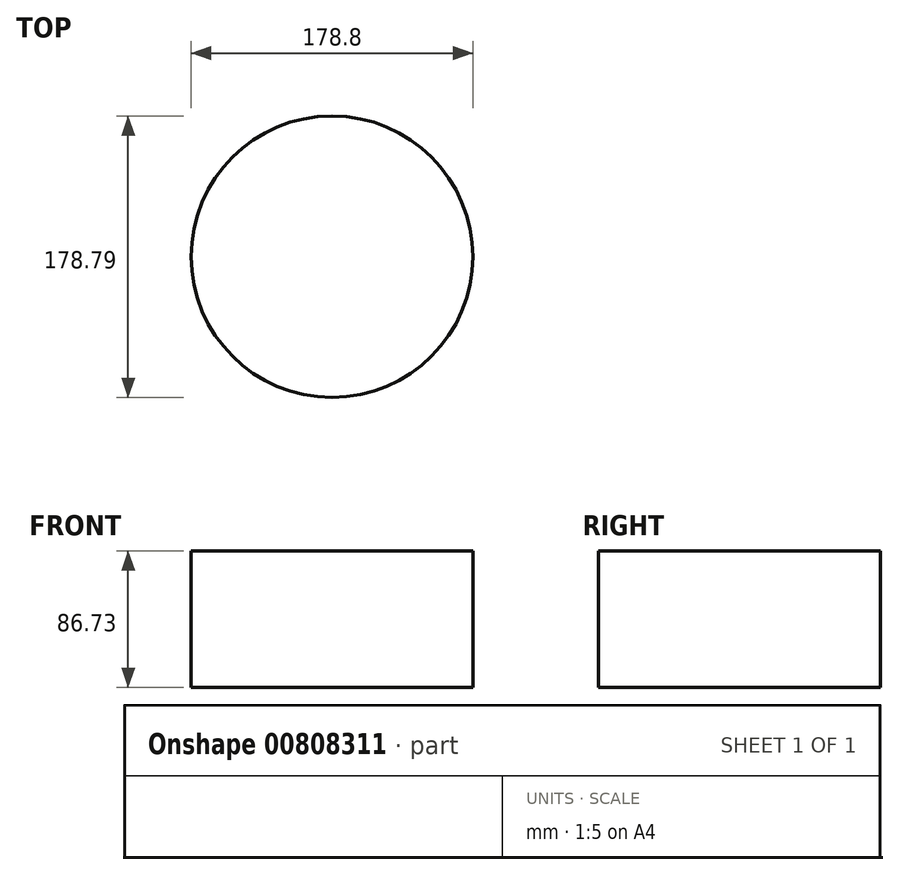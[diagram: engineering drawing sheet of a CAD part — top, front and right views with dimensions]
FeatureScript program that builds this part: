
annotation { "Feature Type Name" : "Feature", "Feature Type Description" : "" }
export const myFeature = defineFeature(function(context is Context, id is Id, definition is map)
    precondition{}
    {
        {
            var Q0;
            Q0=qCreatedBy(makeId("Right.planeOp"),FACE);
            var sketch = newSketch(context, id + "F0", { "sketchPlane" : qUnion([Q0])});
            skLineSegment(sketch, "E0.bottom", {"start": v(-48.15, 39.55) * mm, "end": v(41.24, 39.55) * mm});
            skLineSegment(sketch, "E0.top", {"start": v(-48.15, -47.18) * mm, "end": v(41.24, -47.18) * mm});
            skLineSegment(sketch, "E0.left", {"start": v(-48.15, 39.55) * mm, "end": v(-48.15, -47.18) * mm});
            skLineSegment(sketch, "E0.right", {"start": v(41.24, 39.55) * mm, "end": v(41.24, -47.18) * mm});
            skSolve(sketch);
        }
        {
            var Q0;
            Q0 = qSketchRegion(id + "F0", true);
            var Q1;
            Q1=sQuery(id+"F0.wireOp",EDGE,"E0.left");
            revolve(context, id + "F1", {"surfaceOperationType" : NewSurfaceOperationType.NEW, "entities" : qUnion([Q0]), "axis" : qUnion([Q1]), "revolveType" : RevolveType.FULL});
        }
    });
